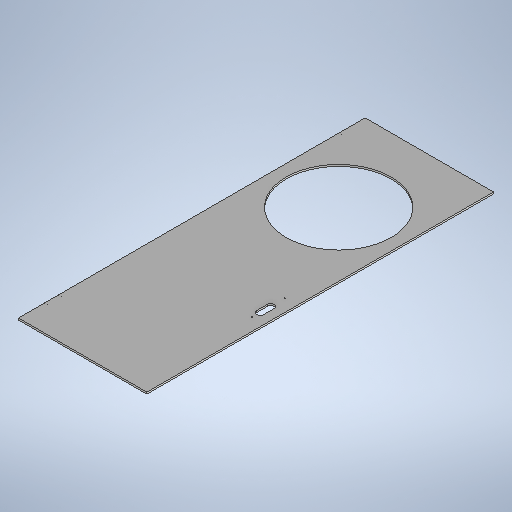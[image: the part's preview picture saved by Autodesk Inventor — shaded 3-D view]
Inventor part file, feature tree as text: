
AUTODESK INVENTOR PART (.ipt)
format: ipt  version: 2025.1 (Build 291241000, 241)  size: 288,768 bytes
history: native  units: mm
features: extrude x5, sketch x4, thread x2, plane x1, mirror x1
ambient origin geometry x8: Origin, YZ Plane, XZ Plane, XY Plane, X Axis, Y Axis, Z Axis, Center Point
bodies: Solid1 (feature_tree)
feature tree (13):
  extrude  "Extrusion1"  Depth=1985.0mm
  extrude  "Extrusion2"  Depth=10.0mm
  sketch  "Sketch6"  dims[d5=519.0mm d6=10.0mm d7=0.0mm]
  extrude  "Extrusion3"  Depth=10.0mm TaperAngle=0.0deg
  extrude  "Extrusion4"  Depth=50.0mm
  extrude  "Extrusion5"  Depth=40.0mm
  thread  "Thread1"  [1 undecoded]
  thread  "Thread2"  [1 undecoded]
  plane  "Work Plane1"
  mirror  "Mirror1"
  sketch  "Sketch4"  dims[d0=735.0mm d1=1985.0mm]
  sketch  "Sketch5"  dims[d2=10.0mm d3=0.0mm d4=600.0mm]
  sketch  "Sketch7"  dims[d8=700.0mm d9=50.0mm d10=40.0mm d11=100.0mm d12=7.0mm d13=60.0mm d14=10.0mm d15=0.0mm d16=187.0mm d17=7.0mm d19=7.0mm d20=0.0mm d21=150.0mm d22=80.0mm d23=6.0mm d24=15.0mm d25=0.0mm d26=10.0mm d27=0.0mm d28=10.0mm d29=0.0mm d30=992.5mm]
note: 2 required parameter values undecoded (feature->parameter linkage not recoverable at this tier; creation-order binding heuristic only, values carry confidence <= 0.55)
